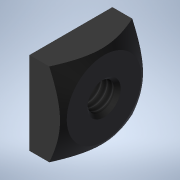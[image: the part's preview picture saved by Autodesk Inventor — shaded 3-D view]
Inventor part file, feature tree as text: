
AUTODESK INVENTOR PART (.ipt)
format: ipt  version: 2021 (Build 250183000, 183)  size: 136,192 bytes
history: native  units: mm
features: sketch x3, revolve x2, thread x1, extrude x1
ambient origin geometry x8: Origin, YZ Plane, XZ Plane, XY Plane, X Axis, Y Axis, Z Axis, Center Point
bodies: Solid1 (feature_tree)
feature tree (7):
  revolve  "Revolution1"  Angle=360.0deg
  revolve  "Revolution2"  [1 undecoded]
  thread  "Thread1"  [1 undecoded]
  extrude  "Extrusion1"  [1 undecoded]
  sketch  "Skizze_1"  dims[d0=360.0deg d1=360.0deg]
  sketch  "Skizze_2"  dims[d2=3.242mm d3=0.0mm d4=4.0mm d5=0.0mm]
  sketch  "Skizze_3"
note: 3 required parameter values undecoded (feature->parameter linkage not recoverable at this tier; creation-order binding heuristic only, values carry confidence <= 0.55)